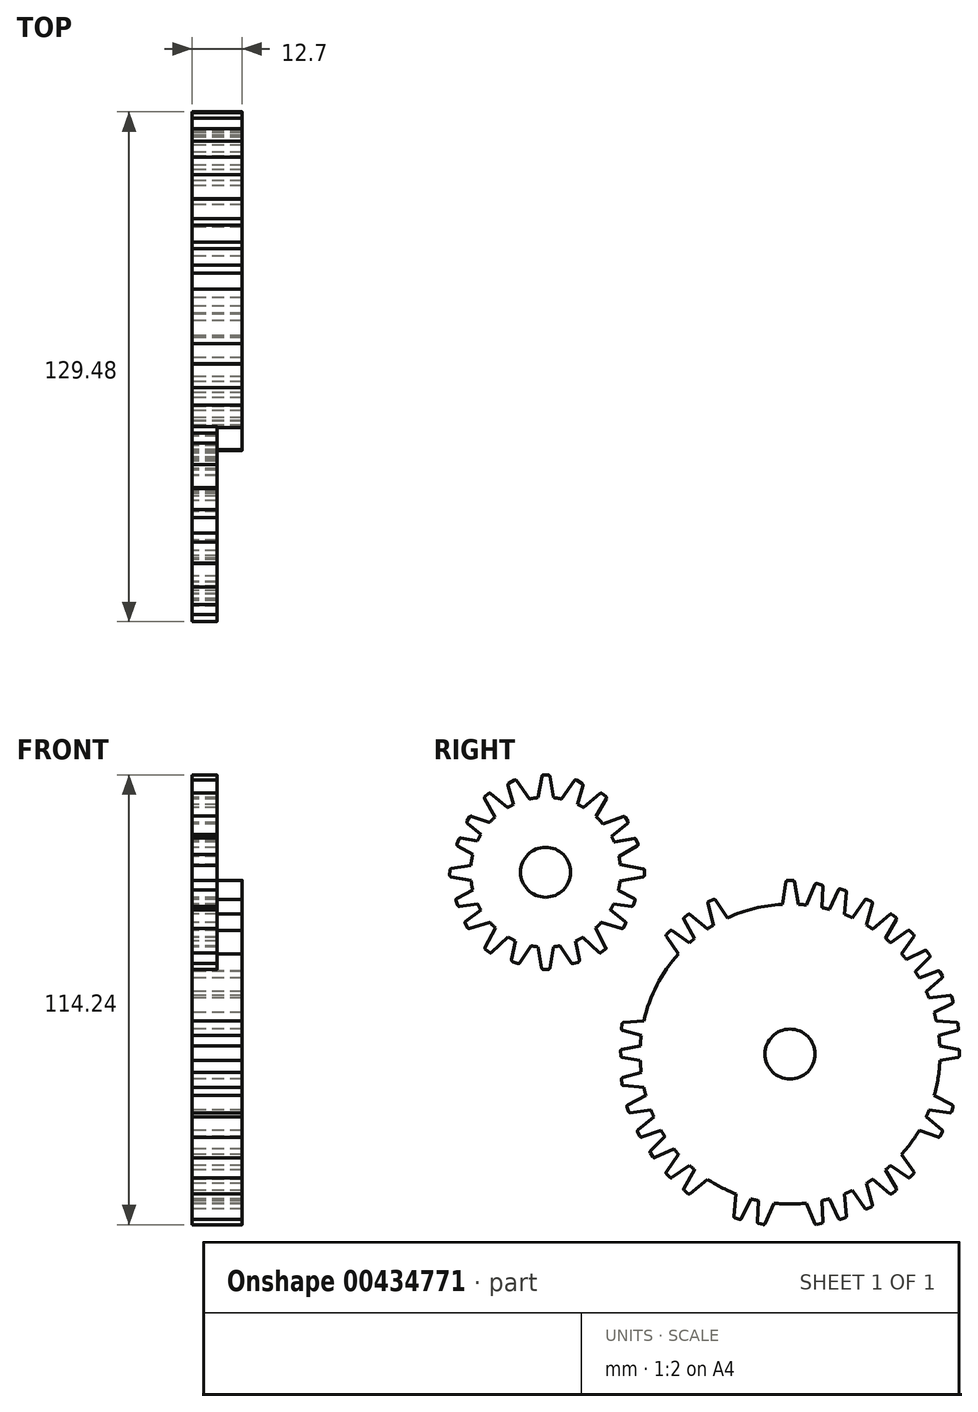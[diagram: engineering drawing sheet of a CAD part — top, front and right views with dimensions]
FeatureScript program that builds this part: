
annotation { "Feature Type Name" : "Feature", "Feature Type Description" : "" }
export const myFeature = defineFeature(function(context is Context, id is Id, definition is map)
    precondition{}
    {
        {
            var Q0;
            Q0=qCreatedBy(makeId("Right.planeOp"),FACE);
            var sketch = newSketch(context, id + "F0", { "sketchPlane" : qUnion([Q0])});
            skCircle(sketch, "E0", {"center": v(0, 0) * mm, "radius": 38.1 * mm});
            skCircle(sketch, "E1", {"center": v(0, 0) * mm, "radius": 6.35 * mm});
            skSolve(sketch);
        }
        {
            var Q0;
            Q0=makeQuery(id+"F0.imprint","IMPRINT",FACE,{"disambiguationData":[TD([[makeQuery(id+"F0.imprint","IMPRINT",EDGE,{"derivedFrom":sQuery(id+"F0.wireOp",EDGE,"E0")}),1.0]])]});
            extrude(context, id + "F1", {"entities" : qUnion([Q0]), "depth" : 12.7 * mm});
        }
        {
            var Q0;
            Q0=qCreatedBy(makeId("Right.planeOp"),FACE);
            var sketch = newSketch(context, id + "F2", { "sketchPlane" : qUnion([Q0])});
            skCircle(sketch, "E2", {"center": v(-62.1, 46.2) * mm, "radius": 19.05 * mm});
            skCircle(sketch, "E3", {"center": v(-62.1, 46.2) * mm, "radius": 6.35 * mm});
            skSolve(sketch);
        }
        {
            var Q0;
            Q0=makeQuery(id+"F2.imprint","IMPRINT",FACE,{"disambiguationData":[TD([[makeQuery(id+"F2.imprint","IMPRINT",EDGE,{"derivedFrom":sQuery(id+"F2.wireOp",EDGE,"E2")}),1.0]])]});
            extrude(context, id + "F3", {"entities" : qUnion([Q0]), "depth" : 6.35 * mm});
        }
        {
            var Q0;
            Q0=qCreatedBy(makeId("Right.planeOp"),FACE);
            var sketch = newSketch(context, id + "F4", { "sketchPlane" : qUnion([Q0])});
            skLineSegment(sketch, "E4", {"start": v(-0.98, 43.83) * mm, "end": v(-2.21, 36.83) * mm});
            skLineSegment(sketch, "E5", {"start": v(2.31, 36.83) * mm, "end": v(-2.21, 36.83) * mm});
            skLineSegment(sketch, "E6", {"start": v(-0.56, 44.17) * mm, "end": v(0.69, 44.15) * mm});
            skPoint(sketch, "E7.visualSharp", {"position": v(-0.91, 44.18) * mm});
            skArc(sketch, "E7.filletArc", {"start": v(-0.56, 44.17) * mm, "mid": v(-0.83, 44.08) * mm, "end": v(-0.98, 43.83) * mm});
            skLineSegment(sketch, "E8", {"start": v(1.08, 43.81) * mm, "end": v(2.31, 36.83) * mm});
            skPoint(sketch, "E9.visualSharp", {"position": v(1.02, 44.14) * mm});
            skArc(sketch, "E9.filletArc", {"start": v(1.08, 43.81) * mm, "mid": v(0.94, 44.05) * mm, "end": v(0.69, 44.15) * mm});
            skArc(sketch, "E10.MirrorCS", {"start": v(-0.56, -44.17) * mm, "mid": v(-0.83, -44.08) * mm, "end": v(-0.98, -43.83) * mm});
            skArc(sketch, "E11.MirrorCS", {"start": v(1.08, -43.81) * mm, "mid": v(0.94, -44.05) * mm, "end": v(0.69, -44.15) * mm});
            skLineSegment(sketch, "E12.MirrorCS", {"start": v(2.31, -36.83) * mm, "end": v(-2.21, -36.83) * mm});
            skLineSegment(sketch, "E13.MirrorCS", {"start": v(-0.56, -44.17) * mm, "end": v(0.69, -44.15) * mm});
            skLineSegment(sketch, "E14.MirrorCS", {"start": v(1.08, -43.81) * mm, "end": v(2.31, -36.83) * mm});
            skLineSegment(sketch, "E15.MirrorCS", {"start": v(-0.98, -43.83) * mm, "end": v(-2.21, -36.83) * mm});
            skPoint(sketch, "E16.MirrorP", {"position": v(1.02, -44.14) * mm});
            skPoint(sketch, "E17.MirrorP", {"position": v(-0.91, -44.18) * mm});
            skPoint(sketch, "E18.center", {"position": v(0, 0) * mm});
            skLineSegment(sketch, "E19.2.0", {"start": v(14.94, 33.36) * mm, "end": v(19.04, 31.44) * mm});
            skLineSegment(sketch, "E19.2.1", {"start": v(20.88, 38.31) * mm, "end": v(19.04, 31.44) * mm});
            skLineSegment(sketch, "E19.2.2", {"start": v(19.01, 39.17) * mm, "end": v(14.94, 33.36) * mm});
            skPoint(sketch, "E19.2.3", {"position": v(19.2, 39.44) * mm});
            skPoint(sketch, "E19.2.4", {"position": v(20.97, 38.66) * mm});
            skArc(sketch, "E19.2.5", {"start": v(19.01, 39.17) * mm, "mid": v(19.24, 39.33) * mm, "end": v(19.5, 39.3) * mm});
            skLineSegment(sketch, "E19.2.6", {"start": v(20.65, 38.8) * mm, "end": v(19.5, 39.3) * mm});
            skArc(sketch, "E19.2.7", {"start": v(20.65, 38.8) * mm, "mid": v(20.85, 38.6) * mm, "end": v(20.88, 38.31) * mm});
            skLineSegment(sketch, "E20.1.0", {"start": v(19.95, 30.9) * mm, "end": v(23.41, 27.99) * mm});
            skPoint(sketch, "E20.1.1", {"position": v(25.64, 35.67) * mm});
            skLineSegment(sketch, "E20.1.2", {"start": v(26.87, 34.68) * mm, "end": v(25.9, 35.46) * mm});
            skLineSegment(sketch, "E20.1.3", {"start": v(26.97, 34.15) * mm, "end": v(23.41, 27.99) * mm});
            skLineSegment(sketch, "E20.1.4", {"start": v(25.38, 35.46) * mm, "end": v(19.95, 30.9) * mm});
            skPoint(sketch, "E20.1.5", {"position": v(27.15, 34.46) * mm});
            skArc(sketch, "E20.1.6", {"start": v(26.87, 34.68) * mm, "mid": v(27.02, 34.43) * mm, "end": v(26.97, 34.15) * mm});
            skArc(sketch, "E20.1.7", {"start": v(25.38, 35.46) * mm, "mid": v(25.64, 35.55) * mm, "end": v(25.9, 35.46) * mm});
            skLineSegment(sketch, "E21", {"start": v(6.32, 43.08) * mm, "end": v(3.55, 36.53) * mm});
            skLineSegment(sketch, "E22", {"start": v(7.96, 35.52) * mm, "end": v(3.55, 36.53) * mm});
            skLineSegment(sketch, "E23", {"start": v(6.8, 43.32) * mm, "end": v(8.01, 43.02) * mm});
            skPoint(sketch, "E24.visualSharp", {"position": v(6.46, 43.41) * mm});
            skArc(sketch, "E24.filletArc", {"start": v(6.8, 43.32) * mm, "mid": v(6.52, 43.3) * mm, "end": v(6.32, 43.08) * mm});
            skLineSegment(sketch, "E25", {"start": v(8.32, 42.6) * mm, "end": v(7.96, 35.52) * mm});
            skPoint(sketch, "E26.visualSharp", {"position": v(8.34, 42.94) * mm});
            skArc(sketch, "E26.filletArc", {"start": v(8.32, 42.6) * mm, "mid": v(8.24, 42.87) * mm, "end": v(8.01, 43.02) * mm});
            skLineSegment(sketch, "E27", {"start": v(12.3, 41.73) * mm, "end": v(9.3, 35.29) * mm});
            skLineSegment(sketch, "E28", {"start": v(13.67, 34.12) * mm, "end": v(9.3, 35.29) * mm});
            skLineSegment(sketch, "E29", {"start": v(12.8, 41.96) * mm, "end": v(14, 41.61) * mm});
            skPoint(sketch, "E30.visualSharp", {"position": v(12.46, 42.06) * mm});
            skArc(sketch, "E30.filletArc", {"start": v(12.8, 41.96) * mm, "mid": v(12.51, 41.94) * mm, "end": v(12.3, 41.73) * mm});
            skLineSegment(sketch, "E31", {"start": v(14.29, 41.19) * mm, "end": v(13.67, 34.12) * mm});
            skPoint(sketch, "E32.visualSharp", {"position": v(14.32, 41.52) * mm});
            skArc(sketch, "E32.filletArc", {"start": v(14.29, 41.19) * mm, "mid": v(14.22, 41.45) * mm, "end": v(14, 41.61) * mm});
            skLineSegment(sketch, "E33", {"start": v(29.97, 31.37) * mm, "end": v(24.14, 27.3) * mm});
            skLineSegment(sketch, "E34", {"start": v(27.34, 24.1) * mm, "end": v(24.14, 27.3) * mm});
            skLineSegment(sketch, "E35", {"start": v(30.51, 31.32) * mm, "end": v(31.37, 30.42) * mm});
            skPoint(sketch, "E36.visualSharp", {"position": v(30.26, 31.58) * mm});
            skArc(sketch, "E36.filletArc", {"start": v(30.51, 31.32) * mm, "mid": v(30.25, 31.44) * mm, "end": v(29.97, 31.37) * mm});
            skLineSegment(sketch, "E37", {"start": v(31.41, 29.9) * mm, "end": v(27.34, 24.1) * mm});
            skPoint(sketch, "E38.visualSharp", {"position": v(31.6, 30.18) * mm});
            skArc(sketch, "E38.filletArc", {"start": v(31.41, 29.9) * mm, "mid": v(31.48, 30.17) * mm, "end": v(31.37, 30.42) * mm});
            skLineSegment(sketch, "E39", {"start": v(34.29, 26.28) * mm, "end": v(27.84, 23.27) * mm});
            skLineSegment(sketch, "E40", {"start": v(30.44, 19.57) * mm, "end": v(27.84, 23.27) * mm});
            skLineSegment(sketch, "E41", {"start": v(34.81, 26.13) * mm, "end": v(35.5, 25.1) * mm});
            skPoint(sketch, "E42.visualSharp", {"position": v(34.61, 26.43) * mm});
            skArc(sketch, "E42.filletArc", {"start": v(34.81, 26.13) * mm, "mid": v(34.58, 26.3) * mm, "end": v(34.29, 26.28) * mm});
            skLineSegment(sketch, "E43", {"start": v(35.46, 24.58) * mm, "end": v(30.44, 19.57) * mm});
            skPoint(sketch, "E44.visualSharp", {"position": v(35.7, 24.82) * mm});
            skArc(sketch, "E44.filletArc", {"start": v(35.46, 24.58) * mm, "mid": v(35.57, 24.83) * mm, "end": v(35.5, 25.1) * mm});
            skLineSegment(sketch, "E45", {"start": v(37.62, 21.1) * mm, "end": v(30.93, 18.66) * mm});
            skLineSegment(sketch, "E46", {"start": v(33.2, 14.74) * mm, "end": v(30.93, 18.66) * mm});
            skLineSegment(sketch, "E47", {"start": v(38.13, 20.9) * mm, "end": v(38.73, 19.81) * mm});
            skPoint(sketch, "E48.visualSharp", {"position": v(37.95, 21.21) * mm});
            skArc(sketch, "E48.filletArc", {"start": v(38.13, 20.9) * mm, "mid": v(37.9, 21.1) * mm, "end": v(37.62, 21.1) * mm});
            skLineSegment(sketch, "E49", {"start": v(38.63, 19.3) * mm, "end": v(33.2, 14.74) * mm});
            skPoint(sketch, "E50.visualSharp", {"position": v(38.89, 19.52) * mm});
            skArc(sketch, "E50.filletArc", {"start": v(38.63, 19.3) * mm, "mid": v(38.77, 19.54) * mm, "end": v(38.73, 19.81) * mm});
            skLineSegment(sketch, "E51", {"start": v(40.6, 14.88) * mm, "end": v(33.55, 14) * mm});
            skLineSegment(sketch, "E52", {"start": v(34.89, 9.67) * mm, "end": v(33.55, 14) * mm});
            skLineSegment(sketch, "E53", {"start": v(41.06, 14.58) * mm, "end": v(41.4, 13.39) * mm});
            skPoint(sketch, "E54.visualSharp", {"position": v(40.96, 14.93) * mm});
            skArc(sketch, "E54.filletArc", {"start": v(41.06, 14.58) * mm, "mid": v(40.89, 14.82) * mm, "end": v(40.6, 14.88) * mm});
            skLineSegment(sketch, "E55", {"start": v(41.2, 12.91) * mm, "end": v(34.89, 9.67) * mm});
            skPoint(sketch, "E56.visualSharp", {"position": v(41.5, 13.07) * mm});
            skArc(sketch, "E56.filletArc", {"start": v(41.2, 12.91) * mm, "mid": v(41.39, 13.11) * mm, "end": v(41.4, 13.39) * mm});
            skLineSegment(sketch, "E57", {"start": v(42.32, 8) * mm, "end": v(35.23, 8.62) * mm});
            skLineSegment(sketch, "E58", {"start": v(35.63, 4.12) * mm, "end": v(35.23, 8.62) * mm});
            skLineSegment(sketch, "E59", {"start": v(42.7, 7.62) * mm, "end": v(42.78, 6.38) * mm});
            skPoint(sketch, "E60.visualSharp", {"position": v(42.67, 7.97) * mm});
            skArc(sketch, "E60.filletArc", {"start": v(42.7, 7.62) * mm, "mid": v(42.58, 7.88) * mm, "end": v(42.32, 8) * mm});
            skLineSegment(sketch, "E61", {"start": v(42.48, 5.96) * mm, "end": v(35.63, 4.12) * mm});
            skPoint(sketch, "E62.visualSharp", {"position": v(42.8, 6.04) * mm});
            skArc(sketch, "E62.filletArc", {"start": v(42.48, 5.96) * mm, "mid": v(42.7, 6.11) * mm, "end": v(42.78, 6.38) * mm});
            skLineSegment(sketch, "E63", {"start": v(42.68, 1.25) * mm, "end": v(35.67, 2.48) * mm});
            skLineSegment(sketch, "E64", {"start": v(35.67, -2.04) * mm, "end": v(35.67, 2.48) * mm});
            skLineSegment(sketch, "E65", {"start": v(43.02, 0.83) * mm, "end": v(43, -0.42) * mm});
            skPoint(sketch, "E66.visualSharp", {"position": v(43.03, 1.18) * mm});
            skArc(sketch, "E66.filletArc", {"start": v(43.02, 0.83) * mm, "mid": v(42.93, 1.1) * mm, "end": v(42.68, 1.25) * mm});
            skLineSegment(sketch, "E67", {"start": v(42.66, -0.8) * mm, "end": v(35.67, -2.04) * mm});
            skPoint(sketch, "E68.visualSharp", {"position": v(43, -0.75) * mm});
            skArc(sketch, "E68.filletArc", {"start": v(42.66, -0.8) * mm, "mid": v(42.9, -0.67) * mm, "end": v(43, -0.42) * mm});
            skLineSegment(sketch, "E69.MirrorCS", {"start": v(-43.02, 0.83) * mm, "end": v(-43, -0.42) * mm});
            skArc(sketch, "E70.MirrorCS", {"start": v(-42.66, -0.8) * mm, "mid": v(-42.9, -0.67) * mm, "end": v(-43, -0.42) * mm});
            skLineSegment(sketch, "E71.MirrorCS", {"start": v(-20.65, 38.8) * mm, "end": v(-19.5, 39.3) * mm});
            skArc(sketch, "E72.MirrorCS", {"start": v(-43.02, 0.83) * mm, "mid": v(-42.93, 1.1) * mm, "end": v(-42.68, 1.25) * mm});
            skLineSegment(sketch, "E73.MirrorCS", {"start": v(-30.51, 31.32) * mm, "end": v(-31.37, 30.42) * mm});
            skArc(sketch, "E74.MirrorCS", {"start": v(-30.51, 31.32) * mm, "mid": v(-30.25, 31.44) * mm, "end": v(-29.97, 31.37) * mm});
            skArc(sketch, "E75.MirrorCS", {"start": v(-20.65, 38.8) * mm, "mid": v(-20.85, 38.6) * mm, "end": v(-20.88, 38.31) * mm});
            skArc(sketch, "E76.MirrorCS", {"start": v(-25.38, 35.46) * mm, "mid": v(-25.64, 35.55) * mm, "end": v(-25.9, 35.46) * mm});
            skLineSegment(sketch, "E77.MirrorCS", {"start": v(-42.7, 7.62) * mm, "end": v(-42.78, 6.38) * mm});
            skArc(sketch, "E78.MirrorCS", {"start": v(-8.32, 42.6) * mm, "mid": v(-8.24, 42.87) * mm, "end": v(-8.01, 43.02) * mm});
            skArc(sketch, "E79.MirrorCS", {"start": v(-41.06, 14.58) * mm, "mid": v(-40.89, 14.82) * mm, "end": v(-40.6, 14.88) * mm});
            skArc(sketch, "E80.MirrorCS", {"start": v(-31.41, 29.9) * mm, "mid": v(-31.48, 30.17) * mm, "end": v(-31.37, 30.42) * mm});
            skArc(sketch, "E81.MirrorCS", {"start": v(-14.29, 41.19) * mm, "mid": v(-14.22, 41.45) * mm, "end": v(-14, 41.61) * mm});
            skLineSegment(sketch, "E82.MirrorCS", {"start": v(-26.87, 34.68) * mm, "end": v(-25.9, 35.46) * mm});
            skArc(sketch, "E83.MirrorCS", {"start": v(-41.2, 12.91) * mm, "mid": v(-41.39, 13.11) * mm, "end": v(-41.4, 13.39) * mm});
            skArc(sketch, "E84.MirrorCS", {"start": v(-35.46, 24.58) * mm, "mid": v(-35.57, 24.83) * mm, "end": v(-35.5, 25.1) * mm});
            skLineSegment(sketch, "E85.MirrorCS", {"start": v(-12.8, 41.96) * mm, "end": v(-14, 41.61) * mm});
            skArc(sketch, "E86.MirrorCS", {"start": v(-19.01, 39.17) * mm, "mid": v(-19.24, 39.33) * mm, "end": v(-19.5, 39.3) * mm});
            skArc(sketch, "E87.MirrorCS", {"start": v(-38.13, 20.9) * mm, "mid": v(-37.9, 21.1) * mm, "end": v(-37.62, 21.1) * mm});
            skArc(sketch, "E88.MirrorCS", {"start": v(-12.8, 41.96) * mm, "mid": v(-12.51, 41.94) * mm, "end": v(-12.3, 41.73) * mm});
            skLineSegment(sketch, "E89.MirrorCS", {"start": v(-6.8, 43.32) * mm, "end": v(-8.01, 43.02) * mm});
            skArc(sketch, "E90.MirrorCS", {"start": v(-6.8, 43.32) * mm, "mid": v(-6.52, 43.3) * mm, "end": v(-6.32, 43.08) * mm});
            skArc(sketch, "E91.MirrorCS", {"start": v(-34.81, 26.13) * mm, "mid": v(-34.58, 26.3) * mm, "end": v(-34.29, 26.28) * mm});
            skArc(sketch, "E92.MirrorCS", {"start": v(-42.48, 5.96) * mm, "mid": v(-42.7, 6.11) * mm, "end": v(-42.78, 6.38) * mm});
            skArc(sketch, "E93.MirrorCS", {"start": v(-26.87, 34.68) * mm, "mid": v(-27.02, 34.43) * mm, "end": v(-26.97, 34.15) * mm});
            skLineSegment(sketch, "E94.MirrorCS", {"start": v(-38.13, 20.9) * mm, "end": v(-38.73, 19.81) * mm});
            skArc(sketch, "E95.MirrorCS", {"start": v(-38.63, 19.3) * mm, "mid": v(-38.77, 19.54) * mm, "end": v(-38.73, 19.81) * mm});
            skLineSegment(sketch, "E96.MirrorCS", {"start": v(-34.81, 26.13) * mm, "end": v(-35.5, 25.1) * mm});
            skArc(sketch, "E97.MirrorCS", {"start": v(-42.7, 7.62) * mm, "mid": v(-42.58, 7.88) * mm, "end": v(-42.32, 8) * mm});
            skLineSegment(sketch, "E98.MirrorCS", {"start": v(-41.06, 14.58) * mm, "end": v(-41.4, 13.39) * mm});
            skPoint(sketch, "E99.MirrorP", {"position": v(-40.96, 14.93) * mm});
            skLineSegment(sketch, "E100.MirrorCS", {"start": v(-26.97, 34.15) * mm, "end": v(-23.41, 27.99) * mm});
            skPoint(sketch, "E101.MirrorP", {"position": v(-34.61, 26.43) * mm});
            skPoint(sketch, "E102.MirrorP", {"position": v(-14.32, 41.52) * mm});
            skLineSegment(sketch, "E103.MirrorCS", {"start": v(-25.38, 35.46) * mm, "end": v(-19.95, 30.9) * mm});
            skLineSegment(sketch, "E104.MirrorCS", {"start": v(-35.67, -2.04) * mm, "end": v(-35.67, 2.48) * mm});
            skPoint(sketch, "E105.MirrorP", {"position": v(-19.2, 39.44) * mm});
            skLineSegment(sketch, "E106.MirrorCS", {"start": v(-12.3, 41.73) * mm, "end": v(-9.3, 35.29) * mm});
            skLineSegment(sketch, "E107.MirrorCS", {"start": v(-41.2, 12.91) * mm, "end": v(-34.89, 9.67) * mm});
            skLineSegment(sketch, "E108.MirrorCS", {"start": v(-34.89, 9.67) * mm, "end": v(-33.55, 14) * mm});
            skLineSegment(sketch, "E109.MirrorCS", {"start": v(-34.29, 26.28) * mm, "end": v(-27.84, 23.27) * mm});
            skLineSegment(sketch, "E110.MirrorCS", {"start": v(-42.48, 5.96) * mm, "end": v(-35.63, 4.12) * mm});
            skLineSegment(sketch, "E111.MirrorCS", {"start": v(-20.88, 38.31) * mm, "end": v(-19.04, 31.44) * mm});
            skLineSegment(sketch, "E112.MirrorCS", {"start": v(-13.67, 34.12) * mm, "end": v(-9.3, 35.29) * mm});
            skPoint(sketch, "E113.MirrorP", {"position": v(-27.15, 34.46) * mm});
            skLineSegment(sketch, "E114.MirrorCS", {"start": v(-37.62, 21.1) * mm, "end": v(-30.93, 18.66) * mm});
            skLineSegment(sketch, "E115.MirrorCS", {"start": v(-31.41, 29.9) * mm, "end": v(-27.34, 24.1) * mm});
            skPoint(sketch, "E116.MirrorP", {"position": v(-42.8, 6.04) * mm});
            skPoint(sketch, "E117.MirrorP", {"position": v(-8.34, 42.94) * mm});
            skPoint(sketch, "E118.MirrorP", {"position": v(-25.64, 35.67) * mm});
            skPoint(sketch, "E119.MirrorP", {"position": v(-6.46, 43.41) * mm});
            skLineSegment(sketch, "E120.MirrorCS", {"start": v(-14.29, 41.19) * mm, "end": v(-13.67, 34.12) * mm});
            skPoint(sketch, "E121.MirrorP", {"position": v(-43.03, 1.18) * mm});
            skPoint(sketch, "E122.MirrorP", {"position": v(-38.89, 19.52) * mm});
            skPoint(sketch, "E123.MirrorP", {"position": v(-31.6, 30.18) * mm});
            skLineSegment(sketch, "E124.MirrorCS", {"start": v(-35.63, 4.12) * mm, "end": v(-35.23, 8.62) * mm});
            skLineSegment(sketch, "E125.MirrorCS", {"start": v(-29.97, 31.37) * mm, "end": v(-24.14, 27.3) * mm});
            skPoint(sketch, "E126.MirrorP", {"position": v(-20.97, 38.66) * mm});
            skPoint(sketch, "E127.MirrorP", {"position": v(-12.46, 42.06) * mm});
            skLineSegment(sketch, "E128.MirrorCS", {"start": v(-33.2, 14.74) * mm, "end": v(-30.93, 18.66) * mm});
            skPoint(sketch, "E129.MirrorP", {"position": v(-43, -0.75) * mm});
            skLineSegment(sketch, "E130.MirrorCS", {"start": v(-6.32, 43.08) * mm, "end": v(-3.55, 36.53) * mm});
            skLineSegment(sketch, "E131.MirrorCS", {"start": v(-40.6, 14.88) * mm, "end": v(-33.55, 14) * mm});
            skLineSegment(sketch, "E132.MirrorCS", {"start": v(-14.94, 33.36) * mm, "end": v(-19.04, 31.44) * mm});
            skLineSegment(sketch, "E133.MirrorCS", {"start": v(-30.44, 19.57) * mm, "end": v(-27.84, 23.27) * mm});
            skLineSegment(sketch, "E134.MirrorCS", {"start": v(-35.46, 24.58) * mm, "end": v(-30.44, 19.57) * mm});
            skLineSegment(sketch, "E135.MirrorCS", {"start": v(-19.95, 30.9) * mm, "end": v(-23.41, 27.99) * mm});
            skLineSegment(sketch, "E136.MirrorCS", {"start": v(-42.66, -0.8) * mm, "end": v(-35.67, -2.04) * mm});
            skLineSegment(sketch, "E137.MirrorCS", {"start": v(-7.96, 35.52) * mm, "end": v(-3.55, 36.53) * mm});
            skPoint(sketch, "E138.MirrorP", {"position": v(-42.67, 7.97) * mm});
            skPoint(sketch, "E139.MirrorP", {"position": v(-30.26, 31.58) * mm});
            skPoint(sketch, "E140.MirrorP", {"position": v(-41.5, 13.07) * mm});
            skLineSegment(sketch, "E141.MirrorCS", {"start": v(-27.34, 24.1) * mm, "end": v(-24.14, 27.3) * mm});
            skLineSegment(sketch, "E142.MirrorCS", {"start": v(-19.01, 39.17) * mm, "end": v(-14.94, 33.36) * mm});
            skPoint(sketch, "E143.MirrorP", {"position": v(-35.7, 24.82) * mm});
            skLineSegment(sketch, "E144.MirrorCS", {"start": v(-42.68, 1.25) * mm, "end": v(-35.67, 2.48) * mm});
            skLineSegment(sketch, "E145.MirrorCS", {"start": v(-38.63, 19.3) * mm, "end": v(-33.2, 14.74) * mm});
            skPoint(sketch, "E146.MirrorP", {"position": v(-37.95, 21.21) * mm});
            skLineSegment(sketch, "E147.MirrorCS", {"start": v(-42.32, 8) * mm, "end": v(-35.23, 8.62) * mm});
            skLineSegment(sketch, "E148.MirrorCS", {"start": v(-8.32, 42.6) * mm, "end": v(-7.96, 35.52) * mm});
            skLineSegment(sketch, "E149.MirrorCS", {"start": v(6.8, -43.32) * mm, "end": v(8.01, -43.02) * mm});
            skArc(sketch, "E150.MirrorCS", {"start": v(42.7, -7.62) * mm, "mid": v(42.58, -7.88) * mm, "end": v(42.32, -8) * mm});
            skLineSegment(sketch, "E151.MirrorCS", {"start": v(42.7, -7.62) * mm, "end": v(42.78, -6.38) * mm});
            skLineSegment(sketch, "E152.MirrorCS", {"start": v(30.51, -31.32) * mm, "end": v(31.37, -30.42) * mm});
            skArc(sketch, "E153.MirrorCS", {"start": v(8.32, -42.6) * mm, "mid": v(8.24, -42.87) * mm, "end": v(8.01, -43.02) * mm});
            skArc(sketch, "E154.MirrorCS", {"start": v(42.48, -5.96) * mm, "mid": v(42.7, -6.11) * mm, "end": v(42.78, -6.38) * mm});
            skArc(sketch, "E155.MirrorCS", {"start": v(31.41, -29.9) * mm, "mid": v(31.48, -30.17) * mm, "end": v(31.37, -30.42) * mm});
            skLineSegment(sketch, "E156.MirrorCS", {"start": v(20.65, -38.8) * mm, "end": v(19.5, -39.3) * mm});
            skLineSegment(sketch, "E157.MirrorCS", {"start": v(41.06, -14.58) * mm, "end": v(41.4, -13.39) * mm});
            skLineSegment(sketch, "E158.MirrorCS", {"start": v(12.8, -41.96) * mm, "end": v(14, -41.61) * mm});
            skArc(sketch, "E159.MirrorCS", {"start": v(25.38, -35.46) * mm, "mid": v(25.64, -35.55) * mm, "end": v(25.9, -35.46) * mm});
            skLineSegment(sketch, "E160.MirrorCS", {"start": v(38.13, -20.9) * mm, "end": v(38.73, -19.81) * mm});
            skArc(sketch, "E161.MirrorCS", {"start": v(35.46, -24.58) * mm, "mid": v(35.57, -24.83) * mm, "end": v(35.5, -25.1) * mm});
            skArc(sketch, "E162.MirrorCS", {"start": v(26.87, -34.68) * mm, "mid": v(27.02, -34.43) * mm, "end": v(26.97, -34.15) * mm});
            skLineSegment(sketch, "E163.MirrorCS", {"start": v(26.87, -34.68) * mm, "end": v(25.9, -35.46) * mm});
            skArc(sketch, "E164.MirrorCS", {"start": v(34.81, -26.13) * mm, "mid": v(34.58, -26.3) * mm, "end": v(34.29, -26.28) * mm});
            skArc(sketch, "E165.MirrorCS", {"start": v(41.2, -12.91) * mm, "mid": v(41.39, -13.11) * mm, "end": v(41.4, -13.39) * mm});
            skArc(sketch, "E166.MirrorCS", {"start": v(30.51, -31.32) * mm, "mid": v(30.25, -31.44) * mm, "end": v(29.97, -31.37) * mm});
            skArc(sketch, "E167.MirrorCS", {"start": v(38.63, -19.3) * mm, "mid": v(38.77, -19.54) * mm, "end": v(38.73, -19.81) * mm});
            skArc(sketch, "E168.MirrorCS", {"start": v(14.29, -41.19) * mm, "mid": v(14.22, -41.45) * mm, "end": v(14, -41.61) * mm});
            skArc(sketch, "E169.MirrorCS", {"start": v(41.06, -14.58) * mm, "mid": v(40.89, -14.82) * mm, "end": v(40.6, -14.88) * mm});
            skArc(sketch, "E170.MirrorCS", {"start": v(19.01, -39.17) * mm, "mid": v(19.24, -39.33) * mm, "end": v(19.5, -39.3) * mm});
            skArc(sketch, "E171.MirrorCS", {"start": v(20.65, -38.8) * mm, "mid": v(20.85, -38.6) * mm, "end": v(20.88, -38.31) * mm});
            skArc(sketch, "E172.MirrorCS", {"start": v(6.8, -43.32) * mm, "mid": v(6.52, -43.3) * mm, "end": v(6.32, -43.08) * mm});
            skArc(sketch, "E173.MirrorCS", {"start": v(38.13, -20.9) * mm, "mid": v(37.9, -21.1) * mm, "end": v(37.62, -21.1) * mm});
            skLineSegment(sketch, "E174.MirrorCS", {"start": v(34.81, -26.13) * mm, "end": v(35.5, -25.1) * mm});
            skArc(sketch, "E175.MirrorCS", {"start": v(12.8, -41.96) * mm, "mid": v(12.51, -41.94) * mm, "end": v(12.3, -41.73) * mm});
            skPoint(sketch, "E176.MirrorP", {"position": v(20.97, -38.66) * mm});
            skPoint(sketch, "E177.MirrorP", {"position": v(12.46, -42.06) * mm});
            skPoint(sketch, "E178.MirrorP", {"position": v(34.61, -26.43) * mm});
            skPoint(sketch, "E179.MirrorP", {"position": v(14.32, -41.52) * mm});
            skLineSegment(sketch, "E180.MirrorCS", {"start": v(31.41, -29.9) * mm, "end": v(27.34, -24.1) * mm});
            skLineSegment(sketch, "E181.MirrorCS", {"start": v(42.48, -5.96) * mm, "end": v(35.63, -4.12) * mm});
            skLineSegment(sketch, "E182.MirrorCS", {"start": v(6.32, -43.08) * mm, "end": v(3.55, -36.53) * mm});
            skPoint(sketch, "E183.MirrorP", {"position": v(27.15, -34.46) * mm});
            skPoint(sketch, "E184.MirrorP", {"position": v(42.8, -6.04) * mm});
            skPoint(sketch, "E185.MirrorP", {"position": v(31.6, -30.18) * mm});
            skPoint(sketch, "E186.MirrorP", {"position": v(40.96, -14.93) * mm});
            skPoint(sketch, "E187.MirrorP", {"position": v(37.95, -21.21) * mm});
            skLineSegment(sketch, "E188.MirrorCS", {"start": v(25.38, -35.46) * mm, "end": v(19.95, -30.9) * mm});
            skLineSegment(sketch, "E189.MirrorCS", {"start": v(27.34, -24.1) * mm, "end": v(24.14, -27.3) * mm});
            skLineSegment(sketch, "E190.MirrorCS", {"start": v(38.63, -19.3) * mm, "end": v(33.2, -14.74) * mm});
            skLineSegment(sketch, "E191.MirrorCS", {"start": v(41.2, -12.91) * mm, "end": v(34.89, -9.67) * mm});
            skLineSegment(sketch, "E192.MirrorCS", {"start": v(8.32, -42.6) * mm, "end": v(7.96, -35.52) * mm});
            skLineSegment(sketch, "E193.MirrorCS", {"start": v(14.29, -41.19) * mm, "end": v(13.67, -34.12) * mm});
            skPoint(sketch, "E194.MirrorP", {"position": v(38.89, -19.52) * mm});
            skLineSegment(sketch, "E195.MirrorCS", {"start": v(19.95, -30.9) * mm, "end": v(23.41, -27.99) * mm});
            skLineSegment(sketch, "E196.MirrorCS", {"start": v(30.44, -19.57) * mm, "end": v(27.84, -23.27) * mm});
            skLineSegment(sketch, "E197.MirrorCS", {"start": v(34.29, -26.28) * mm, "end": v(27.84, -23.27) * mm});
            skLineSegment(sketch, "E198.MirrorCS", {"start": v(19.01, -39.17) * mm, "end": v(14.94, -33.36) * mm});
            skPoint(sketch, "E199.MirrorP", {"position": v(42.67, -7.97) * mm});
            skLineSegment(sketch, "E200.MirrorCS", {"start": v(7.96, -35.52) * mm, "end": v(3.55, -36.53) * mm});
            skLineSegment(sketch, "E201.MirrorCS", {"start": v(29.97, -31.37) * mm, "end": v(24.14, -27.3) * mm});
            skLineSegment(sketch, "E202.MirrorCS", {"start": v(37.62, -21.1) * mm, "end": v(30.93, -18.66) * mm});
            skLineSegment(sketch, "E203.MirrorCS", {"start": v(35.63, -4.12) * mm, "end": v(35.23, -8.62) * mm});
            skPoint(sketch, "E204.MirrorP", {"position": v(30.26, -31.58) * mm});
            skLineSegment(sketch, "E205.MirrorCS", {"start": v(33.2, -14.74) * mm, "end": v(30.93, -18.66) * mm});
            skLineSegment(sketch, "E206.MirrorCS", {"start": v(12.3, -41.73) * mm, "end": v(9.3, -35.29) * mm});
            skLineSegment(sketch, "E207.MirrorCS", {"start": v(13.67, -34.12) * mm, "end": v(9.3, -35.29) * mm});
            skLineSegment(sketch, "E208.MirrorCS", {"start": v(14.94, -33.36) * mm, "end": v(19.04, -31.44) * mm});
            skPoint(sketch, "E209.MirrorP", {"position": v(6.46, -43.41) * mm});
            skPoint(sketch, "E210.MirrorP", {"position": v(35.7, -24.82) * mm});
            skLineSegment(sketch, "E211.MirrorCS", {"start": v(40.6, -14.88) * mm, "end": v(33.55, -14) * mm});
            skPoint(sketch, "E212.MirrorP", {"position": v(41.5, -13.07) * mm});
            skLineSegment(sketch, "E213.MirrorCS", {"start": v(35.46, -24.58) * mm, "end": v(30.44, -19.57) * mm});
            skLineSegment(sketch, "E214.MirrorCS", {"start": v(20.88, -38.31) * mm, "end": v(19.04, -31.44) * mm});
            skLineSegment(sketch, "E215.MirrorCS", {"start": v(26.97, -34.15) * mm, "end": v(23.41, -27.99) * mm});
            skLineSegment(sketch, "E216.MirrorCS", {"start": v(34.89, -9.67) * mm, "end": v(33.55, -14) * mm});
            skLineSegment(sketch, "E217.MirrorCS", {"start": v(42.32, -8) * mm, "end": v(35.23, -8.62) * mm});
            skPoint(sketch, "E218.MirrorP", {"position": v(8.34, -42.94) * mm});
            skPoint(sketch, "E219.MirrorP", {"position": v(25.64, -35.67) * mm});
            skPoint(sketch, "E220.MirrorP", {"position": v(19.2, -39.44) * mm});
            skLineSegment(sketch, "E221.MirrorCS", {"start": v(-26.87, -34.68) * mm, "end": v(-25.9, -35.46) * mm});
            skArc(sketch, "E222.MirrorCS", {"start": v(-42.48, -5.96) * mm, "mid": v(-42.7, -6.11) * mm, "end": v(-42.78, -6.38) * mm});
            skArc(sketch, "E223.MirrorCS", {"start": v(-31.41, -29.9) * mm, "mid": v(-31.48, -30.17) * mm, "end": v(-31.37, -30.42) * mm});
            skArc(sketch, "E224.MirrorCS", {"start": v(-12.8, -41.96) * mm, "mid": v(-12.51, -41.94) * mm, "end": v(-12.3, -41.73) * mm});
            skArc(sketch, "E225.MirrorCS", {"start": v(-20.65, -38.8) * mm, "mid": v(-20.85, -38.6) * mm, "end": v(-20.88, -38.31) * mm});
            skArc(sketch, "E226.MirrorCS", {"start": v(-42.7, -7.62) * mm, "mid": v(-42.58, -7.88) * mm, "end": v(-42.32, -8) * mm});
            skArc(sketch, "E227.MirrorCS", {"start": v(-26.87, -34.68) * mm, "mid": v(-27.02, -34.43) * mm, "end": v(-26.97, -34.15) * mm});
            skArc(sketch, "E228.MirrorCS", {"start": v(-34.81, -26.13) * mm, "mid": v(-34.58, -26.3) * mm, "end": v(-34.29, -26.28) * mm});
            skArc(sketch, "E229.MirrorCS", {"start": v(-38.63, -19.3) * mm, "mid": v(-38.77, -19.54) * mm, "end": v(-38.73, -19.81) * mm});
            skLineSegment(sketch, "E230.MirrorCS", {"start": v(-12.8, -41.96) * mm, "end": v(-14, -41.61) * mm});
            skArc(sketch, "E231.MirrorCS", {"start": v(-41.2, -12.91) * mm, "mid": v(-41.39, -13.11) * mm, "end": v(-41.4, -13.39) * mm});
            skArc(sketch, "E232.MirrorCS", {"start": v(-25.38, -35.46) * mm, "mid": v(-25.64, -35.55) * mm, "end": v(-25.9, -35.46) * mm});
            skLineSegment(sketch, "E233.MirrorCS", {"start": v(-41.06, -14.58) * mm, "end": v(-41.4, -13.39) * mm});
            skArc(sketch, "E234.MirrorCS", {"start": v(-38.13, -20.9) * mm, "mid": v(-37.9, -21.1) * mm, "end": v(-37.62, -21.1) * mm});
            skArc(sketch, "E235.MirrorCS", {"start": v(-14.29, -41.19) * mm, "mid": v(-14.22, -41.45) * mm, "end": v(-14, -41.61) * mm});
            skArc(sketch, "E236.MirrorCS", {"start": v(-19.01, -39.17) * mm, "mid": v(-19.24, -39.33) * mm, "end": v(-19.5, -39.3) * mm});
            skArc(sketch, "E237.MirrorCS", {"start": v(-30.51, -31.32) * mm, "mid": v(-30.25, -31.44) * mm, "end": v(-29.97, -31.37) * mm});
            skArc(sketch, "E238.MirrorCS", {"start": v(-35.46, -24.58) * mm, "mid": v(-35.57, -24.83) * mm, "end": v(-35.5, -25.1) * mm});
            skLineSegment(sketch, "E239.MirrorCS", {"start": v(-6.8, -43.32) * mm, "end": v(-8.01, -43.02) * mm});
            skLineSegment(sketch, "E240.MirrorCS", {"start": v(-38.13, -20.9) * mm, "end": v(-38.73, -19.81) * mm});
            skArc(sketch, "E241.MirrorCS", {"start": v(-6.8, -43.32) * mm, "mid": v(-6.52, -43.3) * mm, "end": v(-6.32, -43.08) * mm});
            skLineSegment(sketch, "E242.MirrorCS", {"start": v(-34.81, -26.13) * mm, "end": v(-35.5, -25.1) * mm});
            skLineSegment(sketch, "E243.MirrorCS", {"start": v(-42.7, -7.62) * mm, "end": v(-42.78, -6.38) * mm});
            skLineSegment(sketch, "E244.MirrorCS", {"start": v(-20.65, -38.8) * mm, "end": v(-19.5, -39.3) * mm});
            skArc(sketch, "E245.MirrorCS", {"start": v(-41.06, -14.58) * mm, "mid": v(-40.89, -14.82) * mm, "end": v(-40.6, -14.88) * mm});
            skLineSegment(sketch, "E246.MirrorCS", {"start": v(-30.51, -31.32) * mm, "end": v(-31.37, -30.42) * mm});
            skArc(sketch, "E247.MirrorCS", {"start": v(-8.32, -42.6) * mm, "mid": v(-8.24, -42.87) * mm, "end": v(-8.01, -43.02) * mm});
            skPoint(sketch, "E248.MirrorP", {"position": v(-8.34, -42.94) * mm});
            skLineSegment(sketch, "E249.MirrorCS", {"start": v(-34.29, -26.28) * mm, "end": v(-27.84, -23.27) * mm});
            skLineSegment(sketch, "E250.MirrorCS", {"start": v(-7.96, -35.52) * mm, "end": v(-3.55, -36.53) * mm});
            skLineSegment(sketch, "E251.MirrorCS", {"start": v(-41.2, -12.91) * mm, "end": v(-34.89, -9.67) * mm});
            skLineSegment(sketch, "E252.MirrorCS", {"start": v(-35.46, -24.58) * mm, "end": v(-30.44, -19.57) * mm});
            skPoint(sketch, "E253.MirrorP", {"position": v(-35.7, -24.82) * mm});
            skPoint(sketch, "E254.MirrorP", {"position": v(-27.15, -34.46) * mm});
            skLineSegment(sketch, "E255.MirrorCS", {"start": v(-33.2, -14.74) * mm, "end": v(-30.93, -18.66) * mm});
            skLineSegment(sketch, "E256.MirrorCS", {"start": v(-29.97, -31.37) * mm, "end": v(-24.14, -27.3) * mm});
            skPoint(sketch, "E257.MirrorP", {"position": v(-34.61, -26.43) * mm});
            skLineSegment(sketch, "E258.MirrorCS", {"start": v(-34.89, -9.67) * mm, "end": v(-33.55, -14) * mm});
            skLineSegment(sketch, "E259.MirrorCS", {"start": v(-27.34, -24.1) * mm, "end": v(-24.14, -27.3) * mm});
            skLineSegment(sketch, "E260.MirrorCS", {"start": v(-19.95, -30.9) * mm, "end": v(-23.41, -27.99) * mm});
            skLineSegment(sketch, "E261.MirrorCS", {"start": v(-37.62, -21.1) * mm, "end": v(-30.93, -18.66) * mm});
            skPoint(sketch, "E262.MirrorP", {"position": v(-25.64, -35.67) * mm});
            skLineSegment(sketch, "E263.MirrorCS", {"start": v(-19.01, -39.17) * mm, "end": v(-14.94, -33.36) * mm});
            skPoint(sketch, "E264.MirrorP", {"position": v(-6.46, -43.41) * mm});
            skPoint(sketch, "E265.MirrorP", {"position": v(-19.2, -39.44) * mm});
            skLineSegment(sketch, "E266.MirrorCS", {"start": v(-6.32, -43.08) * mm, "end": v(-3.55, -36.53) * mm});
            skLineSegment(sketch, "E267.MirrorCS", {"start": v(-26.97, -34.15) * mm, "end": v(-23.41, -27.99) * mm});
            skLineSegment(sketch, "E268.MirrorCS", {"start": v(-13.67, -34.12) * mm, "end": v(-9.3, -35.29) * mm});
            skLineSegment(sketch, "E269.MirrorCS", {"start": v(-42.32, -8) * mm, "end": v(-35.23, -8.62) * mm});
            skPoint(sketch, "E270.MirrorP", {"position": v(-42.67, -7.97) * mm});
            skPoint(sketch, "E271.MirrorP", {"position": v(-31.6, -30.18) * mm});
            skPoint(sketch, "E272.MirrorP", {"position": v(-37.95, -21.21) * mm});
            skLineSegment(sketch, "E273.MirrorCS", {"start": v(-14.29, -41.19) * mm, "end": v(-13.67, -34.12) * mm});
            skLineSegment(sketch, "E274.MirrorCS", {"start": v(-38.63, -19.3) * mm, "end": v(-33.2, -14.74) * mm});
            skLineSegment(sketch, "E275.MirrorCS", {"start": v(-42.48, -5.96) * mm, "end": v(-35.63, -4.12) * mm});
            skPoint(sketch, "E276.MirrorP", {"position": v(-41.5, -13.07) * mm});
            skLineSegment(sketch, "E277.MirrorCS", {"start": v(-35.63, -4.12) * mm, "end": v(-35.23, -8.62) * mm});
            skPoint(sketch, "E278.MirrorP", {"position": v(-30.26, -31.58) * mm});
            skLineSegment(sketch, "E279.MirrorCS", {"start": v(-31.41, -29.9) * mm, "end": v(-27.34, -24.1) * mm});
            skLineSegment(sketch, "E280.MirrorCS", {"start": v(-8.32, -42.6) * mm, "end": v(-7.96, -35.52) * mm});
            skLineSegment(sketch, "E281.MirrorCS", {"start": v(-40.6, -14.88) * mm, "end": v(-33.55, -14) * mm});
            skPoint(sketch, "E282.MirrorP", {"position": v(-20.97, -38.66) * mm});
            skLineSegment(sketch, "E283.MirrorCS", {"start": v(-25.38, -35.46) * mm, "end": v(-19.95, -30.9) * mm});
            skPoint(sketch, "E284.MirrorP", {"position": v(-40.96, -14.93) * mm});
            skPoint(sketch, "E285.MirrorP", {"position": v(-42.8, -6.04) * mm});
            skLineSegment(sketch, "E286.MirrorCS", {"start": v(-14.94, -33.36) * mm, "end": v(-19.04, -31.44) * mm});
            skPoint(sketch, "E287.MirrorP", {"position": v(-14.32, -41.52) * mm});
            skPoint(sketch, "E288.MirrorP", {"position": v(-38.89, -19.52) * mm});
            skPoint(sketch, "E289.MirrorP", {"position": v(-12.46, -42.06) * mm});
            skLineSegment(sketch, "E290.MirrorCS", {"start": v(-12.3, -41.73) * mm, "end": v(-9.3, -35.29) * mm});
            skLineSegment(sketch, "E291.MirrorCS", {"start": v(-20.88, -38.31) * mm, "end": v(-19.04, -31.44) * mm});
            skLineSegment(sketch, "E292.MirrorCS", {"start": v(-30.44, -19.57) * mm, "end": v(-27.84, -23.27) * mm});
            skLineSegment(sketch, "E293.MirrorCS", {"start": v(-53.73, 23.67) * mm, "end": v(-53.73, 23.67) * mm});
            skSolve(sketch);
        }
        {
            var Q0;
            Q0=makeQuery(id+"F4.imprint","IMPRINT",FACE,{"disambiguationData":[TD([[makeQuery(id+"F4.imprint","IMPRINT",EDGE,{"derivedFrom":sQuery(id+"F4.wireOp",EDGE,"E4")}),1.0]])]});
            var Q1;
            Q1=makeQuery(id+"F4.imprint","IMPRINT",FACE,{"disambiguationData":[TD([[makeQuery(id+"F4.imprint","IMPRINT",EDGE,{"derivedFrom":sQuery(id+"F4.wireOp",EDGE,"E10.MirrorCS")}),-1.0]])]});
            var Q2;
            Q2=makeQuery(id+"F4.imprint","IMPRINT",FACE,{"disambiguationData":[TD([[makeQuery(id+"F4.imprint","IMPRINT",EDGE,{"derivedFrom":sQuery(id+"F4.wireOp",EDGE,"E19.2.0")}),1.0]])]});
            var Q3;
            Q3=makeQuery(id+"F4.imprint","IMPRINT",FACE,{"disambiguationData":[TD([[makeQuery(id+"F4.imprint","IMPRINT",EDGE,{"derivedFrom":sQuery(id+"F4.wireOp",EDGE,"E20.1.0")}),1.0]])]});
            var Q4;
            Q4=makeQuery(id+"F4.imprint","IMPRINT",FACE,{"disambiguationData":[TD([[makeQuery(id+"F4.imprint","IMPRINT",EDGE,{"derivedFrom":sQuery(id+"F4.wireOp",EDGE,"E21")}),1.0]])]});
            var Q5;
            Q5=makeQuery(id+"F4.imprint","IMPRINT",FACE,{"disambiguationData":[TD([[makeQuery(id+"F4.imprint","IMPRINT",EDGE,{"derivedFrom":sQuery(id+"F4.wireOp",EDGE,"E27")}),1.0]])]});
            var Q6;
            Q6=makeQuery(id+"F4.imprint","IMPRINT",FACE,{"disambiguationData":[TD([[makeQuery(id+"F4.imprint","IMPRINT",EDGE,{"derivedFrom":sQuery(id+"F4.wireOp",EDGE,"E33")}),1.0]])]});
            var Q7;
            Q7=makeQuery(id+"F4.imprint","IMPRINT",FACE,{"disambiguationData":[TD([[makeQuery(id+"F4.imprint","IMPRINT",EDGE,{"derivedFrom":sQuery(id+"F4.wireOp",EDGE,"E39")}),1.0]])]});
            var Q8;
            Q8=makeQuery(id+"F4.imprint","IMPRINT",FACE,{"disambiguationData":[TD([[makeQuery(id+"F4.imprint","IMPRINT",EDGE,{"derivedFrom":sQuery(id+"F4.wireOp",EDGE,"E45")}),1.0]])]});
            var Q9;
            Q9=makeQuery(id+"F4.imprint","IMPRINT",FACE,{"disambiguationData":[TD([[makeQuery(id+"F4.imprint","IMPRINT",EDGE,{"derivedFrom":sQuery(id+"F4.wireOp",EDGE,"E51")}),1.0]])]});
            var Q10;
            Q10=makeQuery(id+"F4.imprint","IMPRINT",FACE,{"disambiguationData":[TD([[makeQuery(id+"F4.imprint","IMPRINT",EDGE,{"derivedFrom":sQuery(id+"F4.wireOp",EDGE,"E57")}),1.0]])]});
            var Q11;
            Q11=makeQuery(id+"F4.imprint","IMPRINT",FACE,{"disambiguationData":[TD([[makeQuery(id+"F4.imprint","IMPRINT",EDGE,{"derivedFrom":sQuery(id+"F4.wireOp",EDGE,"E63")}),1.0]])]});
            var Q12;
            Q12=makeQuery(id+"F4.imprint","IMPRINT",FACE,{"disambiguationData":[TD([[makeQuery(id+"F4.imprint","IMPRINT",EDGE,{"derivedFrom":sQuery(id+"F4.wireOp",EDGE,"E69.MirrorCS")}),1.0]])]});
            var Q13;
            Q13=makeQuery(id+"F4.imprint","IMPRINT",FACE,{"disambiguationData":[TD([[makeQuery(id+"F4.imprint","IMPRINT",EDGE,{"derivedFrom":sQuery(id+"F4.wireOp",EDGE,"E71.MirrorCS")}),-1.0]])]});
            var Q14;
            Q14=makeQuery(id+"F4.imprint","IMPRINT",FACE,{"disambiguationData":[TD([[makeQuery(id+"F4.imprint","IMPRINT",EDGE,{"derivedFrom":sQuery(id+"F4.wireOp",EDGE,"E73.MirrorCS")}),1.0]])]});
            var Q15;
            Q15=makeQuery(id+"F4.imprint","IMPRINT",FACE,{"disambiguationData":[TD([[makeQuery(id+"F4.imprint","IMPRINT",EDGE,{"derivedFrom":sQuery(id+"F4.wireOp",EDGE,"E76.MirrorCS")}),1.0]])]});
            var Q16;
            Q16=makeQuery(id+"F4.imprint","IMPRINT",FACE,{"disambiguationData":[TD([[makeQuery(id+"F4.imprint","IMPRINT",EDGE,{"derivedFrom":sQuery(id+"F4.wireOp",EDGE,"E77.MirrorCS")}),1.0]])]});
            var Q17;
            Q17=makeQuery(id+"F4.imprint","IMPRINT",FACE,{"disambiguationData":[TD([[makeQuery(id+"F4.imprint","IMPRINT",EDGE,{"derivedFrom":sQuery(id+"F4.wireOp",EDGE,"E78.MirrorCS")}),-1.0]])]});
            var Q18;
            Q18=makeQuery(id+"F4.imprint","IMPRINT",FACE,{"disambiguationData":[TD([[makeQuery(id+"F4.imprint","IMPRINT",EDGE,{"derivedFrom":sQuery(id+"F4.wireOp",EDGE,"E79.MirrorCS")}),-1.0]])]});
            var Q19;
            Q19=makeQuery(id+"F4.imprint","IMPRINT",FACE,{"disambiguationData":[TD([[makeQuery(id+"F4.imprint","IMPRINT",EDGE,{"derivedFrom":sQuery(id+"F4.wireOp",EDGE,"E81.MirrorCS")}),-1.0]])]});
            var Q20;
            Q20=makeQuery(id+"F4.imprint","IMPRINT",FACE,{"disambiguationData":[TD([[makeQuery(id+"F4.imprint","IMPRINT",EDGE,{"derivedFrom":sQuery(id+"F4.wireOp",EDGE,"E84.MirrorCS")}),-1.0]])]});
            var Q21;
            Q21=makeQuery(id+"F4.imprint","IMPRINT",FACE,{"disambiguationData":[TD([[makeQuery(id+"F4.imprint","IMPRINT",EDGE,{"derivedFrom":sQuery(id+"F4.wireOp",EDGE,"E87.MirrorCS")}),-1.0]])]});
            var Q22;
            Q22=makeQuery(id+"F4.imprint","IMPRINT",FACE,{"disambiguationData":[TD([[makeQuery(id+"F4.imprint","IMPRINT",EDGE,{"derivedFrom":sQuery(id+"F4.wireOp",EDGE,"E149.MirrorCS")}),1.0]])]});
            var Q23;
            Q23=makeQuery(id+"F4.imprint","IMPRINT",FACE,{"disambiguationData":[TD([[makeQuery(id+"F4.imprint","IMPRINT",EDGE,{"derivedFrom":sQuery(id+"F4.wireOp",EDGE,"E150.MirrorCS")}),-1.0]])]});
            var Q24;
            Q24=makeQuery(id+"F4.imprint","IMPRINT",FACE,{"disambiguationData":[TD([[makeQuery(id+"F4.imprint","IMPRINT",EDGE,{"derivedFrom":sQuery(id+"F4.wireOp",EDGE,"E152.MirrorCS")}),1.0]])]});
            var Q25;
            Q25=makeQuery(id+"F4.imprint","IMPRINT",FACE,{"disambiguationData":[TD([[makeQuery(id+"F4.imprint","IMPRINT",EDGE,{"derivedFrom":sQuery(id+"F4.wireOp",EDGE,"E156.MirrorCS")}),-1.0]])]});
            var Q26;
            Q26=makeQuery(id+"F4.imprint","IMPRINT",FACE,{"disambiguationData":[TD([[makeQuery(id+"F4.imprint","IMPRINT",EDGE,{"derivedFrom":sQuery(id+"F4.wireOp",EDGE,"E157.MirrorCS")}),1.0]])]});
            var Q27;
            Q27=makeQuery(id+"F4.imprint","IMPRINT",FACE,{"disambiguationData":[TD([[makeQuery(id+"F4.imprint","IMPRINT",EDGE,{"derivedFrom":sQuery(id+"F4.wireOp",EDGE,"E158.MirrorCS")}),1.0]])]});
            var Q28;
            Q28=makeQuery(id+"F4.imprint","IMPRINT",FACE,{"disambiguationData":[TD([[makeQuery(id+"F4.imprint","IMPRINT",EDGE,{"derivedFrom":sQuery(id+"F4.wireOp",EDGE,"E159.MirrorCS")}),1.0]])]});
            var Q29;
            Q29=makeQuery(id+"F4.imprint","IMPRINT",FACE,{"disambiguationData":[TD([[makeQuery(id+"F4.imprint","IMPRINT",EDGE,{"derivedFrom":sQuery(id+"F4.wireOp",EDGE,"E160.MirrorCS")}),1.0]])]});
            var Q30;
            Q30=makeQuery(id+"F4.imprint","IMPRINT",FACE,{"disambiguationData":[TD([[makeQuery(id+"F4.imprint","IMPRINT",EDGE,{"derivedFrom":sQuery(id+"F4.wireOp",EDGE,"E161.MirrorCS")}),-1.0]])]});
            var Q31;
            Q31=makeQuery(id+"F4.imprint","IMPRINT",FACE,{"disambiguationData":[TD([[makeQuery(id+"F4.imprint","IMPRINT",EDGE,{"derivedFrom":sQuery(id+"F4.wireOp",EDGE,"E221.MirrorCS")}),1.0]])]});
            var Q32;
            Q32=makeQuery(id+"F4.imprint","IMPRINT",FACE,{"disambiguationData":[TD([[makeQuery(id+"F4.imprint","IMPRINT",EDGE,{"derivedFrom":sQuery(id+"F4.wireOp",EDGE,"E222.MirrorCS")}),1.0]])]});
            var Q33;
            Q33=makeQuery(id+"F4.imprint","IMPRINT",FACE,{"disambiguationData":[TD([[makeQuery(id+"F4.imprint","IMPRINT",EDGE,{"derivedFrom":sQuery(id+"F4.wireOp",EDGE,"E223.MirrorCS")}),1.0]])]});
            var Q34;
            Q34=makeQuery(id+"F4.imprint","IMPRINT",FACE,{"disambiguationData":[TD([[makeQuery(id+"F4.imprint","IMPRINT",EDGE,{"derivedFrom":sQuery(id+"F4.wireOp",EDGE,"E224.MirrorCS")}),1.0]])]});
            var Q35;
            Q35=makeQuery(id+"F4.imprint","IMPRINT",FACE,{"disambiguationData":[TD([[makeQuery(id+"F4.imprint","IMPRINT",EDGE,{"derivedFrom":sQuery(id+"F4.wireOp",EDGE,"E225.MirrorCS")}),-1.0]])]});
            var Q36;
            Q36=makeQuery(id+"F4.imprint","IMPRINT",FACE,{"disambiguationData":[TD([[makeQuery(id+"F4.imprint","IMPRINT",EDGE,{"derivedFrom":sQuery(id+"F4.wireOp",EDGE,"E228.MirrorCS")}),1.0]])]});
            var Q37;
            Q37=makeQuery(id+"F4.imprint","IMPRINT",FACE,{"disambiguationData":[TD([[makeQuery(id+"F4.imprint","IMPRINT",EDGE,{"derivedFrom":sQuery(id+"F4.wireOp",EDGE,"E229.MirrorCS")}),1.0]])]});
            var Q38;
            Q38=makeQuery(id+"F4.imprint","IMPRINT",FACE,{"disambiguationData":[TD([[makeQuery(id+"F4.imprint","IMPRINT",EDGE,{"derivedFrom":sQuery(id+"F4.wireOp",EDGE,"E231.MirrorCS")}),1.0]])]});
            var Q39;
            Q39=makeQuery(id+"F4.imprint","IMPRINT",FACE,{"disambiguationData":[TD([[makeQuery(id+"F4.imprint","IMPRINT",EDGE,{"derivedFrom":sQuery(id+"F4.wireOp",EDGE,"E239.MirrorCS")}),-1.0]])]});
            var Q40;
            Q40=makeQuery(id+"F4.imprint","IMPRINT",FACE,{"disambiguationData":[TD([[makeQuery(id+"F4.imprint","IMPRINT",EDGE,{"derivedFrom":sQuery(id+"F4.wireOp",EDGE,"e277809f-37f8-4dd5-94ea-24f88f2b4f8c")}),1.0]])]});
            var Q41;
            Q41=makeQuery(id+"F4.imprint","IMPRINT",FACE,{"disambiguationData":[TD([[makeQuery(id+"F4.imprint","IMPRINT",EDGE,{"derivedFrom":sQuery(id+"F4.wireOp",EDGE,"f132e469-9755-4257-ad4d-92abcd36ffad")}),1.0]])]});
            var Q42;
            Q42=makeQuery(id+"F4.imprint","IMPRINT",FACE,{"disambiguationData":[TD([[makeQuery(id+"F4.imprint","IMPRINT",EDGE,{"derivedFrom":sQuery(id+"F4.wireOp",EDGE,"ac3523e3-4e2f-4fcd-91f9-94241e715077")}),1.0]])]});
            var Q43;
            Q43=makeQuery(id+"F4.imprint","IMPRINT",FACE,{"disambiguationData":[TD([[makeQuery(id+"F4.imprint","IMPRINT",EDGE,{"derivedFrom":sQuery(id+"F4.wireOp",EDGE,"286a2b35-f1ce-4ccf-864d-4838354aa3a8")}),1.0]])]});
            var Q44;
            Q44=makeQuery(id+"F4.imprint","IMPRINT",FACE,{"disambiguationData":[TD([[makeQuery(id+"F4.imprint","IMPRINT",EDGE,{"derivedFrom":sQuery(id+"F4.wireOp",EDGE,"b29db0df-deba-42d4-8cec-b0382ae1f66e")}),1.0]])]});
            var Q45;
            Q45=makeQuery(id+"F4.imprint","IMPRINT",FACE,{"disambiguationData":[TD([[makeQuery(id+"F4.imprint","IMPRINT",EDGE,{"derivedFrom":sQuery(id+"F4.wireOp",EDGE,"71b3b59b-7d24-4007-9fb4-6533f0d12968")}),1.0]])]});
            var Q46;
            Q46=makeQuery(id+"F4.imprint","IMPRINT",FACE,{"disambiguationData":[TD([[makeQuery(id+"F4.imprint","IMPRINT",EDGE,{"derivedFrom":sQuery(id+"F4.wireOp",EDGE,"37d11830-3382-4254-bf88-2b00bc85477f")}),-1.0]])]});
            var Q47;
            Q47=makeQuery(id+"F4.imprint","IMPRINT",FACE,{"disambiguationData":[TD([[makeQuery(id+"F4.imprint","IMPRINT",EDGE,{"derivedFrom":sQuery(id+"F4.wireOp",EDGE,"7e5b9a53-3252-4699-b08f-4789624d0d06")}),1.0]])]});
            var Q48;
            Q48=makeQuery(id+"F4.imprint","IMPRINT",FACE,{"disambiguationData":[TD([[makeQuery(id+"F4.imprint","IMPRINT",EDGE,{"derivedFrom":sQuery(id+"F4.wireOp",EDGE,"3b1b0b71-2313-4383-8283-3e555ca834442.MirrorCS")}),-1.0]])]});
            var Q49;
            Q49=makeQuery(id+"F4.imprint","IMPRINT",FACE,{"disambiguationData":[TD([[makeQuery(id+"F4.imprint","IMPRINT",EDGE,{"derivedFrom":sQuery(id+"F4.wireOp",EDGE,"3b1b0b71-2313-4383-8283-3e555ca834449.MirrorCS")}),-1.0]])]});
            var Q50;
            Q50=makeQuery(id+"F4.imprint","IMPRINT",FACE,{"disambiguationData":[TD([[makeQuery(id+"F4.imprint","IMPRINT",EDGE,{"derivedFrom":sQuery(id+"F4.wireOp",EDGE,"3b1b0b71-2313-4383-8283-3e555ca8344411.MirrorCS")}),-1.0]])]});
            var Q51;
            Q51=makeQuery(id+"F4.imprint","IMPRINT",FACE,{"disambiguationData":[TD([[makeQuery(id+"F4.imprint","IMPRINT",EDGE,{"derivedFrom":sQuery(id+"F4.wireOp",EDGE,"3b1b0b71-2313-4383-8283-3e555ca8344415.MirrorCS")}),1.0]])]});
            var Q52;
            Q52=makeQuery(id+"F4.imprint","IMPRINT",FACE,{"disambiguationData":[TD([[makeQuery(id+"F4.imprint","IMPRINT",EDGE,{"derivedFrom":sQuery(id+"F4.wireOp",EDGE,"1fac3fa2-fcb0-4391-b6bf-820a2dd73d670.MirrorCS")}),-1.0]])]});
            var Q53;
            Q53=makeQuery(id+"F4.imprint","IMPRINT",FACE,{"disambiguationData":[TD([[makeQuery(id+"F4.imprint","IMPRINT",EDGE,{"derivedFrom":sQuery(id+"F4.wireOp",EDGE,"1fac3fa2-fcb0-4391-b6bf-820a2dd73d672.MirrorCS")}),-1.0]])]});
            var Q54;
            Q54=makeQuery(id+"F4.imprint","IMPRINT",FACE,{"disambiguationData":[TD([[makeQuery(id+"F4.imprint","IMPRINT",EDGE,{"derivedFrom":sQuery(id+"F4.wireOp",EDGE,"1fac3fa2-fcb0-4391-b6bf-820a2dd73d673.MirrorCS")}),-1.0]])]});
            var Q55;
            Q55=makeQuery(id+"F4.imprint","IMPRINT",FACE,{"disambiguationData":[TD([[makeQuery(id+"F4.imprint","IMPRINT",EDGE,{"derivedFrom":sQuery(id+"F4.wireOp",EDGE,"01122786-1439-4d1a-a0e1-852a5f2d40c80.MirrorCS")}),1.0]])]});
            var Q56;
            Q56=makeQuery(id+"F4.imprint","IMPRINT",FACE,{"disambiguationData":[TD([[makeQuery(id+"F4.imprint","IMPRINT",EDGE,{"derivedFrom":sQuery(id+"F4.wireOp",EDGE,"01122786-1439-4d1a-a0e1-852a5f2d40c82.MirrorCS")}),1.0]])]});
            var Q57;
            Q57=makeQuery(id+"F4.imprint","IMPRINT",FACE,{"disambiguationData":[TD([[makeQuery(id+"F4.imprint","IMPRINT",EDGE,{"derivedFrom":sQuery(id+"F4.wireOp",EDGE,"01122786-1439-4d1a-a0e1-852a5f2d40c84.MirrorCS")}),1.0]])]});
            var Q58;
            Q58=makeQuery(id+"F4.imprint","IMPRINT",FACE,{"disambiguationData":[TD([[makeQuery(id+"F4.imprint","IMPRINT",EDGE,{"derivedFrom":sQuery(id+"F4.wireOp",EDGE,"01122786-1439-4d1a-a0e1-852a5f2d40c814.MirrorCS")}),1.0]])]});
            var Q59;
            Q59=makeQuery(id+"F4.imprint","IMPRINT",FACE,{"disambiguationData":[TD([[makeQuery(id+"F4.imprint","IMPRINT",EDGE,{"derivedFrom":sQuery(id+"F4.wireOp",EDGE,"1fac3fa2-fcb0-4391-b6bf-820a2dd73d671.MirrorCS")}),-1.0]])]});
            extrude(context, id + "F5", {"entities" : qUnion([Q0, Q1, Q2, Q3, Q4, Q5, Q6, Q7, Q8, Q9, Q10, Q11, Q12, Q13, Q14, Q15, Q16, Q17, Q18, Q19, Q20, Q21, Q22, Q23, Q24, Q25, Q26, Q27, Q28, Q29, Q30, Q31, Q32, Q33, Q34, Q35, Q36, Q37, Q38, Q39, Q40, Q41, Q42, Q43, Q44, Q45, Q46, Q47, Q48, Q49, Q50, Q51, Q52, Q53, Q54, Q55, Q56, Q57, Q58, Q59]), "depth" : 12.7 * mm});
        }
        {
            var Q0;
            Q0=qCreatedBy(makeId("Right.planeOp"),FACE);
            var sketch = newSketch(context, id + "F6", { "sketchPlane" : qUnion([Q0])});
            skLineSegment(sketch, "E294", {"start": v(-63.08, 70.55) * mm, "end": v(-64.32, 63.55) * mm});
            skLineSegment(sketch, "E295", {"start": v(-59.8, 63.55) * mm, "end": v(-64.32, 63.55) * mm});
            skLineSegment(sketch, "E296", {"start": v(-62.66, 70.9) * mm, "end": v(-61.42, 70.87) * mm});
            skPoint(sketch, "E297.visualSharp", {"position": v(-63.02, 70.9) * mm});
            skArc(sketch, "E297.filletArc", {"start": v(-62.66, 70.9) * mm, "mid": v(-62.94, 70.8) * mm, "end": v(-63.08, 70.55) * mm});
            skLineSegment(sketch, "E298", {"start": v(-61.03, 70.54) * mm, "end": v(-59.8, 63.55) * mm});
            skPoint(sketch, "E299.visualSharp", {"position": v(-61.08, 70.87) * mm});
            skArc(sketch, "E299.filletArc", {"start": v(-61.03, 70.54) * mm, "mid": v(-61.16, 70.78) * mm, "end": v(-61.42, 70.87) * mm});
            skLineSegment(sketch, "E300", {"start": v(-71.63, 68.28) * mm, "end": v(-69.94, 61.96) * mm});
            skLineSegment(sketch, "E301", {"start": v(-65.63, 63.98) * mm, "end": v(-69.94, 61.96) * mm});
            skLineSegment(sketch, "E302", {"start": v(-71.48, 68.7) * mm, "end": v(-70.06, 69.63) * mm});
            skPoint(sketch, "E303.visualSharp", {"position": v(-71.7, 68.55) * mm});
            skArc(sketch, "E303.filletArc", {"start": v(-71.48, 68.7) * mm, "mid": v(-71.62, 68.52) * mm, "end": v(-71.63, 68.28) * mm});
            skLineSegment(sketch, "E304", {"start": v(-69.5, 69.52) * mm, "end": v(-65.63, 63.98) * mm});
            skPoint(sketch, "E305.visualSharp", {"position": v(-69.73, 69.84) * mm});
            skArc(sketch, "E305.filletArc", {"start": v(-69.5, 69.52) * mm, "mid": v(-69.76, 69.69) * mm, "end": v(-70.06, 69.63) * mm});
            skLineSegment(sketch, "E306", {"start": v(-37.3, 47.1) * mm, "end": v(-44.3, 48.33) * mm});
            skLineSegment(sketch, "E307", {"start": v(-44.3, 43.8) * mm, "end": v(-44.3, 48.33) * mm});
            skLineSegment(sketch, "E308", {"start": v(-36.96, 46.68) * mm, "end": v(-36.99, 45.43) * mm});
            skPoint(sketch, "E309.visualSharp", {"position": v(-36.95, 47.04) * mm});
            skArc(sketch, "E309.filletArc", {"start": v(-36.96, 46.68) * mm, "mid": v(-37.06, 46.95) * mm, "end": v(-37.3, 47.1) * mm});
            skLineSegment(sketch, "E310", {"start": v(-37.32, 45.04) * mm, "end": v(-44.3, 43.8) * mm});
            skPoint(sketch, "E311.visualSharp", {"position": v(-37, 45.1) * mm});
            skArc(sketch, "E311.filletArc", {"start": v(-37.32, 45.04) * mm, "mid": v(-37.08, 45.18) * mm, "end": v(-36.99, 45.43) * mm});
            skLineSegment(sketch, "E312", {"start": v(-86.11, 45.04) * mm, "end": v(-79.1, 43.8) * mm});
            skLineSegment(sketch, "E313", {"start": v(-79.1, 48.33) * mm, "end": v(-79.1, 43.8) * mm});
            skLineSegment(sketch, "E314", {"start": v(-86.46, 45.47) * mm, "end": v(-86.43, 46.7) * mm});
            skPoint(sketch, "E315.visualSharp", {"position": v(-86.47, 45.1) * mm});
            skArc(sketch, "E315.filletArc", {"start": v(-86.46, 45.47) * mm, "mid": v(-86.36, 45.2) * mm, "end": v(-86.11, 45.04) * mm});
            skLineSegment(sketch, "E316", {"start": v(-86.1, 47.1) * mm, "end": v(-79.1, 48.33) * mm});
            skPoint(sketch, "E317.visualSharp", {"position": v(-86.42, 47.04) * mm});
            skArc(sketch, "E317.filletArc", {"start": v(-86.1, 47.1) * mm, "mid": v(-86.33, 46.96) * mm, "end": v(-86.43, 46.7) * mm});
            skLineSegment(sketch, "E318", {"start": v(-61.03, 21.85) * mm, "end": v(-59.8, 28.85) * mm});
            skLineSegment(sketch, "E319", {"start": v(-64.32, 28.85) * mm, "end": v(-59.8, 28.85) * mm});
            skLineSegment(sketch, "E320", {"start": v(-61.45, 21.5) * mm, "end": v(-62.7, 21.53) * mm});
            skPoint(sketch, "E321.visualSharp", {"position": v(-61.1, 21.5) * mm});
            skArc(sketch, "E321.filletArc", {"start": v(-61.45, 21.5) * mm, "mid": v(-61.18, 21.6) * mm, "end": v(-61.03, 21.85) * mm});
            skLineSegment(sketch, "E322", {"start": v(-63.08, 21.86) * mm, "end": v(-64.32, 28.85) * mm});
            skPoint(sketch, "E323.visualSharp", {"position": v(-63.03, 21.54) * mm});
            skArc(sketch, "E323.filletArc", {"start": v(-63.08, 21.86) * mm, "mid": v(-62.95, 21.63) * mm, "end": v(-62.7, 21.53) * mm});
            skLineSegment(sketch, "E324", {"start": v(-77.63, 64.89) * mm, "end": v(-74.07, 58.73) * mm});
            skLineSegment(sketch, "E325", {"start": v(-70.6, 61.63) * mm, "end": v(-74.07, 58.73) * mm});
            skLineSegment(sketch, "E326", {"start": v(-77.53, 65.42) * mm, "end": v(-76.56, 66.2) * mm});
            skPoint(sketch, "E327.visualSharp", {"position": v(-77.8, 65.2) * mm});
            skArc(sketch, "E327.filletArc", {"start": v(-77.53, 65.42) * mm, "mid": v(-77.68, 65.17) * mm, "end": v(-77.63, 64.89) * mm});
            skLineSegment(sketch, "E328", {"start": v(-76.04, 66.2) * mm, "end": v(-70.6, 61.63) * mm});
            skPoint(sketch, "E329.visualSharp", {"position": v(-76.3, 66.4) * mm});
            skArc(sketch, "E329.filletArc", {"start": v(-76.04, 66.2) * mm, "mid": v(-76.3, 66.3) * mm, "end": v(-76.56, 66.2) * mm});
            skLineSegment(sketch, "E330", {"start": v(-81.93, 58.64) * mm, "end": v(-76.45, 54.1) * mm});
            skLineSegment(sketch, "E331", {"start": v(-74.22, 58.04) * mm, "end": v(-76.45, 54.1) * mm});
            skLineSegment(sketch, "E332", {"start": v(-82.02, 59.18) * mm, "end": v(-81.39, 60.24) * mm});
            skPoint(sketch, "E333.visualSharp", {"position": v(-82.2, 58.87) * mm});
            skArc(sketch, "E333.filletArc", {"start": v(-82.02, 59.18) * mm, "mid": v(-82.08, 58.9) * mm, "end": v(-81.93, 58.64) * mm});
            skLineSegment(sketch, "E334", {"start": v(-80.9, 60.42) * mm, "end": v(-74.22, 58.04) * mm});
            skPoint(sketch, "E335.visualSharp", {"position": v(-81.22, 60.53) * mm});
            skArc(sketch, "E335.filletArc", {"start": v(-80.9, 60.42) * mm, "mid": v(-81.18, 60.42) * mm, "end": v(-81.39, 60.24) * mm});
            skLineSegment(sketch, "E336", {"start": v(-84.42, 52.92) * mm, "end": v(-78.26, 49.36) * mm});
            skLineSegment(sketch, "E337", {"start": v(-76.71, 53.61) * mm, "end": v(-78.26, 49.36) * mm});
            skLineSegment(sketch, "E338", {"start": v(-84.6, 53.43) * mm, "end": v(-84.15, 54.6) * mm});
            skPoint(sketch, "E339.visualSharp", {"position": v(-84.73, 53.1) * mm});
            skArc(sketch, "E339.filletArc", {"start": v(-84.6, 53.43) * mm, "mid": v(-84.6, 53.14) * mm, "end": v(-84.42, 52.92) * mm});
            skLineSegment(sketch, "E340", {"start": v(-83.7, 54.85) * mm, "end": v(-76.71, 53.61) * mm});
            skPoint(sketch, "E341.visualSharp", {"position": v(-84.03, 54.9) * mm});
            skArc(sketch, "E341.filletArc", {"start": v(-83.7, 54.85) * mm, "mid": v(-83.97, 54.8) * mm, "end": v(-84.15, 54.6) * mm});
            skPoint(sketch, "E342.startSnap0", {"position": v(-79.1, 46.07) * mm});
            skArc(sketch, "E343.MirrorCS", {"start": v(-84.87, 39) * mm, "mid": v(-84.87, 39.3) * mm, "end": v(-84.67, 39.51) * mm});
            skArc(sketch, "E344.MirrorCS", {"start": v(-84.03, 37.56) * mm, "mid": v(-84.3, 37.62) * mm, "end": v(-84.47, 37.83) * mm});
            skLineSegment(sketch, "E345.MirrorCS", {"start": v(-84.87, 39) * mm, "end": v(-84.47, 37.83) * mm});
            skPoint(sketch, "E346.MirrorP", {"position": v(-84.36, 37.52) * mm});
            skPoint(sketch, "E347.MirrorP", {"position": v(-84.99, 39.35) * mm});
            skArc(sketch, "E348.MirrorCS", {"start": v(-82.51, 33.17) * mm, "mid": v(-82.55, 33.46) * mm, "end": v(-82.4, 33.7) * mm});
            skLineSegment(sketch, "E349.MirrorCS", {"start": v(-82.51, 33.17) * mm, "end": v(-81.91, 32.08) * mm});
            skArc(sketch, "E350.MirrorCS", {"start": v(-75.8, 25.84) * mm, "mid": v(-76.05, 25.73) * mm, "end": v(-76.32, 25.8) * mm});
            skArc(sketch, "E351.MirrorCS", {"start": v(-81.44, 31.89) * mm, "mid": v(-81.71, 31.9) * mm, "end": v(-81.91, 32.08) * mm});
            skLineSegment(sketch, "E352.MirrorCS", {"start": v(-77.32, 26.54) * mm, "end": v(-76.32, 25.8) * mm});
            skArc(sketch, "E353.MirrorCS", {"start": v(-77.32, 26.54) * mm, "mid": v(-77.48, 26.78) * mm, "end": v(-77.45, 27.07) * mm});
            skLineSegment(sketch, "E354.MirrorCS", {"start": v(-64.98, 28.77) * mm, "end": v(-69.33, 30.46) * mm});
            skLineSegment(sketch, "E355.MirrorCS", {"start": v(-81.44, 31.89) * mm, "end": v(-74.67, 34.01) * mm});
            skLineSegment(sketch, "E356.MirrorCS", {"start": v(-84.67, 39.51) * mm, "end": v(-78.38, 42.84) * mm});
            skLineSegment(sketch, "E357.MirrorCS", {"start": v(-68.62, 23.22) * mm, "end": v(-64.98, 28.77) * mm});
            skPoint(sketch, "E358.MirrorP", {"position": v(-77.61, 26.75) * mm});
            skLineSegment(sketch, "E359.MirrorCS", {"start": v(-74.67, 34.01) * mm, "end": v(-76.75, 38.03) * mm});
            skLineSegment(sketch, "E360.MirrorCS", {"start": v(-84.03, 37.56) * mm, "end": v(-77, 38.53) * mm});
            skLineSegment(sketch, "E361.MirrorCS", {"start": v(-77.45, 27.07) * mm, "end": v(-74.2, 33.4) * mm});
            skLineSegment(sketch, "E362.MirrorCS", {"start": v(-82.4, 33.7) * mm, "end": v(-76.75, 38.03) * mm});
            skLineSegment(sketch, "E363.MirrorCS", {"start": v(-70.6, 30.67) * mm, "end": v(-74.2, 33.4) * mm});
            skPoint(sketch, "E364.MirrorP", {"position": v(-76.04, 25.61) * mm});
            skLineSegment(sketch, "E365.MirrorCS", {"start": v(-75.8, 25.84) * mm, "end": v(-70.6, 30.67) * mm});
            skPoint(sketch, "E366.MirrorP", {"position": v(-81.75, 31.79) * mm});
            skLineSegment(sketch, "E367.MirrorCS", {"start": v(-70.72, 24.02) * mm, "end": v(-69.33, 30.46) * mm});
            skLineSegment(sketch, "E368.MirrorCS", {"start": v(-77, 38.53) * mm, "end": v(-78.38, 42.84) * mm});
            skPoint(sketch, "E369.MirrorP", {"position": v(-82.68, 33.49) * mm});
            skArc(sketch, "E370.MirrorCS", {"start": v(-46.76, 65.42) * mm, "mid": v(-46.61, 65.17) * mm, "end": v(-46.66, 64.89) * mm});
            skArc(sketch, "E371.MirrorCS", {"start": v(-52.81, 68.7) * mm, "mid": v(-52.67, 68.52) * mm, "end": v(-52.65, 68.28) * mm});
            skArc(sketch, "E372.MirrorCS", {"start": v(-38.66, 53.35) * mm, "mid": v(-38.66, 53.06) * mm, "end": v(-38.84, 52.84) * mm});
            skArc(sketch, "E373.MirrorCS", {"start": v(-41.24, 59.1) * mm, "mid": v(-41.18, 58.8) * mm, "end": v(-41.33, 58.56) * mm});
            skLineSegment(sketch, "E374.MirrorCS", {"start": v(-38.66, 53.35) * mm, "end": v(-39.1, 54.5) * mm});
            skArc(sketch, "E375.MirrorCS", {"start": v(-42.36, 60.34) * mm, "mid": v(-42.08, 60.34) * mm, "end": v(-41.87, 60.16) * mm});
            skArc(sketch, "E376.MirrorCS", {"start": v(-48.25, 66.2) * mm, "mid": v(-47.99, 66.3) * mm, "end": v(-47.73, 66.2) * mm});
            skArc(sketch, "E377.MirrorCS", {"start": v(-39.56, 54.76) * mm, "mid": v(-39.29, 54.72) * mm, "end": v(-39.1, 54.5) * mm});
            skLineSegment(sketch, "E378.MirrorCS", {"start": v(-52.81, 68.7) * mm, "end": v(-54.22, 69.63) * mm});
            skArc(sketch, "E379.MirrorCS", {"start": v(-54.78, 69.52) * mm, "mid": v(-54.52, 69.69) * mm, "end": v(-54.22, 69.63) * mm});
            skLineSegment(sketch, "E380.MirrorCS", {"start": v(-41.24, 59.1) * mm, "end": v(-41.87, 60.16) * mm});
            skLineSegment(sketch, "E381.MirrorCS", {"start": v(-46.76, 65.42) * mm, "end": v(-47.73, 66.2) * mm});
            skLineSegment(sketch, "E382.MirrorCS", {"start": v(-49.05, 57.96) * mm, "end": v(-46.81, 54.03) * mm});
            skLineSegment(sketch, "E383.MirrorCS", {"start": v(-41.33, 58.56) * mm, "end": v(-46.81, 54.03) * mm});
            skPoint(sketch, "E384.MirrorP", {"position": v(-42.04, 60.45) * mm});
            skPoint(sketch, "E385.MirrorP", {"position": v(-41.05, 58.78) * mm});
            skLineSegment(sketch, "E386.MirrorCS", {"start": v(-46.66, 64.89) * mm, "end": v(-50.22, 58.73) * mm});
            skPoint(sketch, "E387.MirrorP", {"position": v(-52.58, 68.55) * mm});
            skPoint(sketch, "E388.MirrorP", {"position": v(-46.48, 65.2) * mm});
            skPoint(sketch, "E389.MirrorP", {"position": v(-38.53, 53.02) * mm});
            skLineSegment(sketch, "E390.MirrorCS", {"start": v(-52.65, 68.28) * mm, "end": v(-54.35, 61.96) * mm});
            skPoint(sketch, "E391.MirrorP", {"position": v(-54.55, 69.84) * mm});
            skLineSegment(sketch, "E392.MirrorCS", {"start": v(-42.36, 60.34) * mm, "end": v(-49.05, 57.96) * mm});
            skLineSegment(sketch, "E393.MirrorCS", {"start": v(-48.25, 66.2) * mm, "end": v(-53.68, 61.63) * mm});
            skPoint(sketch, "E394.MirrorP", {"position": v(-47.99, 66.4) * mm});
            skLineSegment(sketch, "E395.MirrorCS", {"start": v(-38.84, 52.84) * mm, "end": v(-45, 49.28) * mm});
            skPoint(sketch, "E396.MirrorP", {"position": v(-39.23, 54.82) * mm});
            skLineSegment(sketch, "E397.MirrorCS", {"start": v(-39.56, 54.76) * mm, "end": v(-46.55, 53.53) * mm});
            skLineSegment(sketch, "E398.MirrorCS", {"start": v(-54.78, 69.52) * mm, "end": v(-58.66, 63.98) * mm});
            skLineSegment(sketch, "E399.MirrorCS", {"start": v(-53.68, 61.63) * mm, "end": v(-50.22, 58.73) * mm});
            skLineSegment(sketch, "E400.MirrorCS", {"start": v(-58.66, 63.98) * mm, "end": v(-54.35, 61.96) * mm});
            skLineSegment(sketch, "E401.MirrorCS", {"start": v(-46.55, 53.53) * mm, "end": v(-45, 49.28) * mm});
            skLineSegment(sketch, "E402.MirrorCS", {"start": v(-39.42, 39) * mm, "end": v(-39.82, 37.83) * mm});
            skArc(sketch, "E403.MirrorCS", {"start": v(-40.26, 37.56) * mm, "mid": v(-40, 37.62) * mm, "end": v(-39.82, 37.83) * mm});
            skArc(sketch, "E404.MirrorCS", {"start": v(-39.42, 39) * mm, "mid": v(-39.42, 39.3) * mm, "end": v(-39.62, 39.51) * mm});
            skArc(sketch, "E405.MirrorCS", {"start": v(-46.97, 26.54) * mm, "mid": v(-46.8, 26.78) * mm, "end": v(-46.84, 27.07) * mm});
            skLineSegment(sketch, "E406.MirrorCS", {"start": v(-46.97, 26.54) * mm, "end": v(-47.97, 25.8) * mm});
            skArc(sketch, "E407.MirrorCS", {"start": v(-42.85, 31.89) * mm, "mid": v(-42.58, 31.9) * mm, "end": v(-42.37, 32.08) * mm});
            skArc(sketch, "E408.MirrorCS", {"start": v(-48.49, 25.84) * mm, "mid": v(-48.24, 25.73) * mm, "end": v(-47.97, 25.8) * mm});
            skLineSegment(sketch, "E409.MirrorCS", {"start": v(-41.78, 33.17) * mm, "end": v(-42.37, 32.08) * mm});
            skArc(sketch, "E410.MirrorCS", {"start": v(-41.78, 33.17) * mm, "mid": v(-41.74, 33.46) * mm, "end": v(-41.9, 33.7) * mm});
            skLineSegment(sketch, "E411.MirrorCS", {"start": v(-48.49, 25.84) * mm, "end": v(-53.69, 30.67) * mm});
            skPoint(sketch, "E412.MirrorP", {"position": v(-41.6, 33.49) * mm});
            skLineSegment(sketch, "E413.MirrorCS", {"start": v(-53.69, 30.67) * mm, "end": v(-50.08, 33.4) * mm});
            skPoint(sketch, "E414.MirrorP", {"position": v(-42.53, 31.79) * mm});
            skLineSegment(sketch, "E415.MirrorCS", {"start": v(-41.9, 33.7) * mm, "end": v(-47.54, 38.03) * mm});
            skPoint(sketch, "E416.MirrorP", {"position": v(-48.24, 25.61) * mm});
            skLineSegment(sketch, "E417.MirrorCS", {"start": v(-46.84, 27.07) * mm, "end": v(-50.08, 33.4) * mm});
            skPoint(sketch, "E418.MirrorP", {"position": v(-52.93, 23.68) * mm});
            skLineSegment(sketch, "E419.MirrorCS", {"start": v(-40.26, 37.56) * mm, "end": v(-47.3, 38.53) * mm});
            skPoint(sketch, "E420.MirrorP", {"position": v(-46.68, 26.75) * mm});
            skLineSegment(sketch, "E421.MirrorCS", {"start": v(-49.62, 34.01) * mm, "end": v(-47.54, 38.03) * mm});
            skLineSegment(sketch, "E422.MirrorCS", {"start": v(-55.67, 23.23) * mm, "end": v(-59.3, 28.77) * mm});
            skLineSegment(sketch, "E423.MirrorCS", {"start": v(-39.62, 39.51) * mm, "end": v(-45.9, 42.84) * mm});
            skLineSegment(sketch, "E424.MirrorCS", {"start": v(-59.3, 28.77) * mm, "end": v(-54.92, 30.52) * mm});
            skPoint(sketch, "E425.MirrorP", {"position": v(-39.3, 39.35) * mm});
            skPoint(sketch, "E426.MirrorP", {"position": v(-39.93, 37.52) * mm});
            skLineSegment(sketch, "E427.MirrorCS", {"start": v(-42.85, 31.89) * mm, "end": v(-49.62, 34.01) * mm});
            skLineSegment(sketch, "E428.MirrorCS", {"start": v(-53.51, 23.97) * mm, "end": v(-54.92, 30.52) * mm});
            skLineSegment(sketch, "E429.MirrorCS", {"start": v(-47.3, 38.53) * mm, "end": v(-45.9, 42.84) * mm});
            skLineSegment(sketch, "E430", {"start": v(-53.91, 23.31) * mm, "end": v(-55.06, 23) * mm});
            skPoint(sketch, "E431.visualSharp", {"position": v(-55.45, 22.9) * mm});
            skArc(sketch, "E431.filletArc", {"start": v(-55.67, 23.23) * mm, "mid": v(-55.4, 23.02) * mm, "end": v(-55.06, 23) * mm});
            skLineSegment(sketch, "E432", {"start": v(-69.21, 23.02) * mm, "end": v(-70.39, 23.43) * mm});
            skPoint(sketch, "E433.visualSharp", {"position": v(-68.84, 22.9) * mm});
            skArc(sketch, "E433.filletArc", {"start": v(-69.21, 23.02) * mm, "mid": v(-68.88, 23.02) * mm, "end": v(-68.62, 23.22) * mm});
            skArc(sketch, "E434.filletArc", {"start": v(-70.72, 24.02) * mm, "mid": v(-70.66, 23.66) * mm, "end": v(-70.39, 23.43) * mm});
            skPoint(sketch, "E435.visualSharp", {"position": v(-53.4, 23.45) * mm});
            skArc(sketch, "E435.filletArc", {"start": v(-53.91, 23.31) * mm, "mid": v(-53.58, 23.56) * mm, "end": v(-53.51, 23.97) * mm});
            skSolve(sketch);
        }
        {
            var Q0;
            Q0 = qSketchRegion(id + "F6", true);
            var Q1;
            Q1=makeQuery(id+"F1.opExtrude","CAP_FACE",FACE,{"disambiguationData":[OSD([sQuery(id+"F0.wireOp",EDGE,"E0"),sQuery(id+"F0.wireOp",EDGE,"E1")])],"isStart":true});
            extrude(context, id + "F7", {"entities" : qUnion([Q0, Q1]), "operationType" : NewBodyOperationType.ADD, "depth" : 6.35 * mm});
        }
    });
